# Revit family: IS_iLifeA_T5258_BIM_GB
name_source: partatom
category: Plumbing Fixtures
units: mm (PartAtom-declared; Revit-internal decimal feet)

## family parameters
Always vertical = No
Cut with Voids When Loaded = No
OmniClass Number = 23.45.05.14.21.11
OmniClass Title = Bath/Shower Units
Part Type = Normal
Room Calculation Point = No
Round Connector Dimension = Use Diameter
Shared = No
Work Plane-Based = No

## types (7) — shared parameters
Accessories = https://www.idealstandard.co.uk
AreaUnits = milliliters
BIMObjectName = IS_IdealStandard_BathroomCabinets_I.Life A_T5258
BIMobject category = Other Sanitary
BIMobject category code = other-sanitary
BIMobject main category = Sanitary
BIMobject main category code = sanitary
Brand = Ideal Standard
Brand url = http://www.idealstandard.co.uk
ConnectionType = Plumbing
CurrencyUnit = £
CurrentRevision = 1
Date of publishing = 11/03/2022
Description = I.Life A Vanity Unit 2 Drawers 120cm
DurationUnit = Years
Edition number = 1
ElementType = Bathroom Furniture
Features = Vanity Unit 2 Drawers 120cm
Help = https://www.idealstandard.co.uk
IFC Classification = Sanitary Terminal
IfcExportAs = IfcFurnitureType
IfcExportType = BATHROOMCABINET
Installation instructions = https://www.idealstandard.co.uk
InstallationInstructions = https://www.idealstandard.co.uk
LinearUnits = millilitres
MaintenanceInformation = https://www.idealstandard.co.uk
Manufacturer = Ideal Standard
Manufacturer name = Ideal Standard
ManufacturerURL = https://www.idealstandard.co.uk
Masterformat 2014 Code = 12 50 00
Masterformat 2014 Description = Furniture
Material = Wood
Material main = MDF
ModelReference = I.Life A Vanity Unit 2 Drawers 120cm
NBS Reference Code = 45-35-72/318
NBS Reference Description = Bathroom Cabinets
Name = BathroomCabinets_I.Life A_T5258_IdealStandard
NettWeight = 42.41127968
NominalDepth = 460 mm
NominalHeight = 630 mm  [stored 2.06693 ft]
NominalLength = 460 mm
NominalWidth = 1200 mm
OmniClass Code = 23-31 25 13
OmniClass Description = Bathroom Cabinets
PredefinedType = Bathroom Furniture
Product Guid = 1e748190-042e-478b-8b53-ecadd671d1b2
Product SKU = T5258
Product certification = https://www.idealstandard.co.uk
Product data url = https://bimobject.com
Product family = I.life
Product group = Bathroom Furniture
Product name = I.Life A Vanity Unit 2 Drawers 120cm
Product url = https://www.idealstandard.co.uk
ProductInformation = https://www.idealstandard.co.uk
QR code = http://bimobject.com
Shape = rectangular
Size = 1200 x 460 x 630 mm
Space = Internal
SpareParts = https://www.idealstandard.co.uk
Technical description = https://www.idealstandard.co.uk
UNSPSC Code = 301815
URL = https://www.idealstandard.co.uk
Uniclass 1.4 Code = L8241
Uniclass 1.4 Description = Bathroom cabinets
Uniclass 2.0 Code = PR-35-75-08
Uniclass 2.0 Description = Bathroom Cabinets
Uniclass 2015 Code = Pr_40_30_78_05
Uniclass 2015 Name = Bathroom furniture
Uniclass2015Code = Pr_40_30_87_03
Uniclass2015Title = Bathroom cabinets
Uniclass2015Version = v1.25
Version = 1
VolumeUnits = Litres
WRASURL = https://www.wrasapprovals.co.uk
WarrantyDescription = manufacturer warranty
WarrantyDurationUnit = years
Youtube clip = https://www.youtube.com
zero-valued in all types: MaterialThickness

## per-type parameters (varying)
| type | BarCode | Color | Finish | GTIN code | MainColor | Model | ModelNumber |
| T5258DU - I.Life A Vanity Unit 2 Drawers 120cm - Matt White | 8014140502036 | Matt White | Matt White | https://8014140502036 | Matt White | T5258DU | T5258DU |
| T5258NF - I.Life A Vanity Unit 2 Drawers 120cm - Sand Beige Matt | 8014140493624 | Sand Beige Matt | Sand Beige Matt | https://8014140493624 | Sand Beige Matt | T5258NF | T5258NF |
| T5258NG - I.Life A Vanity Unit 2 Drawers 120cm - Quartz Grey Matt | 8014140493631 | Quartz Grey Matt | Quartz Grey Matt | https://8014140493631 | Quartz Grey Matt | T5258NG | T5258NG |
| T5258NV - I.Life A Vanity Unit 2 Drawers 120cm - Carbon Grey Matt | 8014140493655 | Carbon Grey Matt | Carbon Grey Matt | https://8014140493655 | Carbon Grey Matt | T5258NV | T5258NV |
| T5258NH - I.Life A Vanity Unit 2 Drawers 120cm - Greige Matt | 8014140493648 | Greige Matt | Greige Matt | https://8014140493648 | Greige Matt | T5258NH | T5258NH |
| T5258NX - I.Life A Vanity Unit 2 Drawers 120cm - Natural Oak | 8014140502050 | Natural Oak | Natural Oak | https://8014140502050 | Natural Oak | T5258NX | T5258NX |
| T5258NW - I.Life A Vanity Unit 2 Drawers 120cm - Coffee Oak | 8014140502043 | Coffee Oak | Coffee Oak | https://8014140502043 | Coffee Oak | T5258NW | T5258NW |

note: [stored X ft] marks values corroborated as IEEE doubles in the binary element streams (Revit-internal decimal feet)

## geometry (parser evidence)
native form markers: Sweep x3
no freeform markers — native parametric forms only
